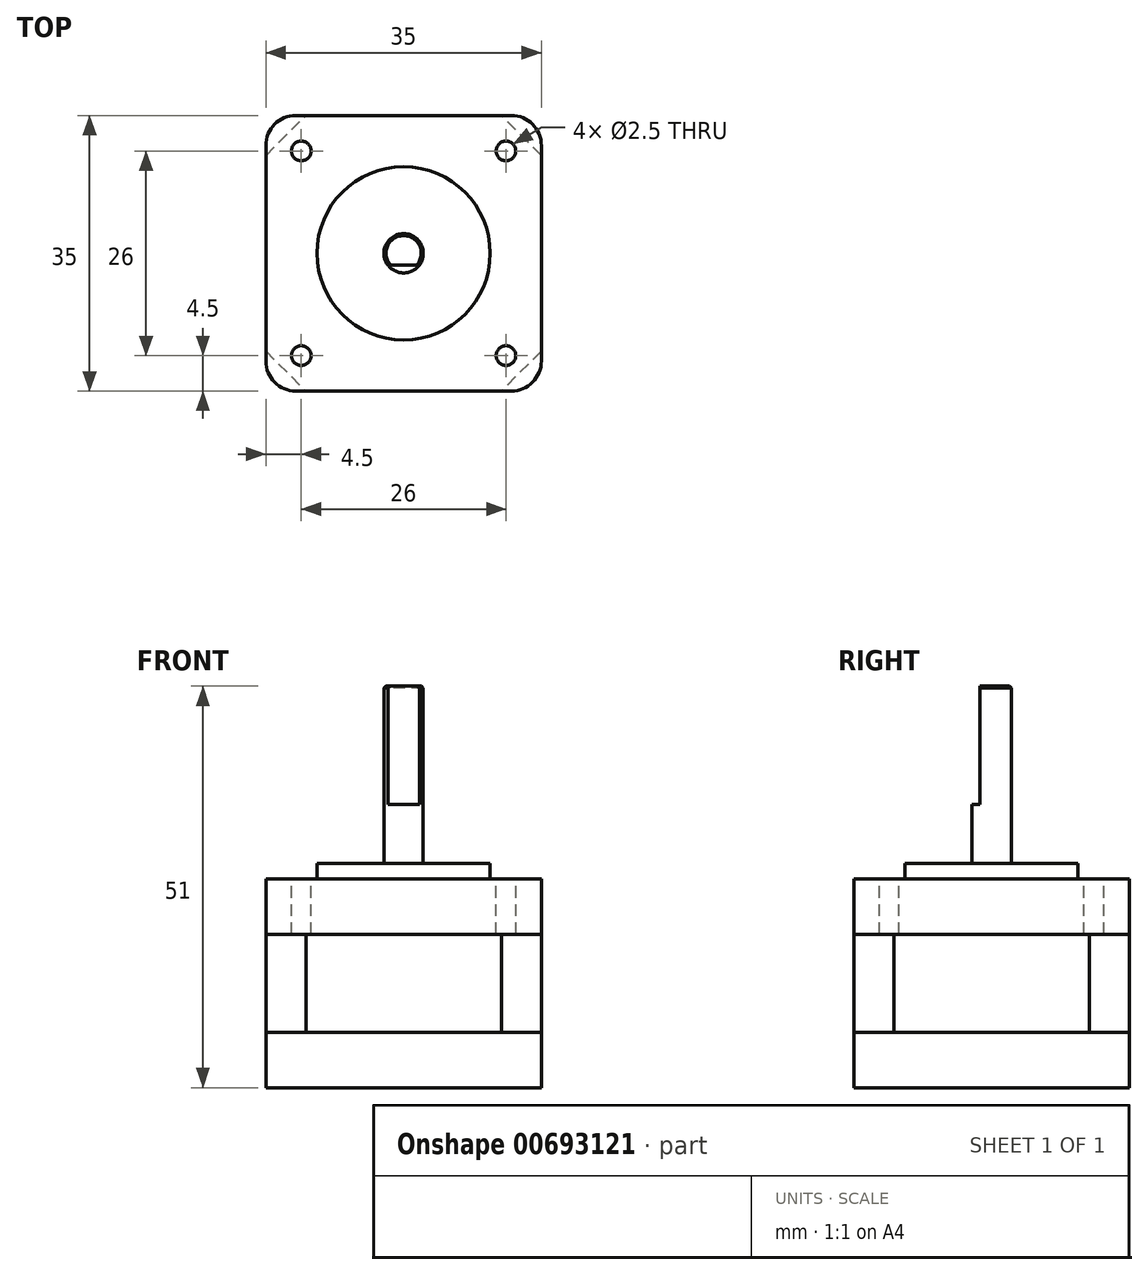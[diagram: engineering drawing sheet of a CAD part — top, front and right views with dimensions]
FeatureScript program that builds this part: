
annotation { "Feature Type Name" : "Feature", "Feature Type Description" : "" }
export const myFeature = defineFeature(function(context is Context, id is Id, definition is map)
    precondition{}
    {
        {
            var Q0;
            Q0=qCreatedBy(makeId("Top.planeOp"),FACE);
            var sketch = newSketch(context, id + "F0", { "sketchPlane" : qUnion([Q0])});
            skLineSegment(sketch, "E0.bottom", {"start": v(17.5, -17.5) * mm, "end": v(-17.5, -17.5) * mm});
            skLineSegment(sketch, "E0.top", {"start": v(17.5, 17.5) * mm, "end": v(-17.5, 17.5) * mm});
            skLineSegment(sketch, "E0.left", {"start": v(17.5, -17.5) * mm, "end": v(17.5, 17.5) * mm});
            skLineSegment(sketch, "E0.right", {"start": v(-17.5, -17.5) * mm, "end": v(-17.5, 17.5) * mm});
            skPoint(sketch, "E0.middle", {"position": v(0, 0) * mm});
            skPoint(sketch, "E1", {"position": v(-13, 13) * mm});
            skPoint(sketch, "E2.MirrorP", {"position": v(13, 13) * mm});
            skPoint(sketch, "E3.MirrorP", {"position": v(-13, -13) * mm});
            skPoint(sketch, "E4.MirrorP", {"position": v(13, -13) * mm});
            skCircle(sketch, "E5", {"center": v(0, 0) * mm, "radius": 11 * mm});
            skSolve(sketch);
        }
        {
            var Q0;
            Q0=makeQuery(id+"F0.imprint","IMPRINT",FACE,{"disambiguationData":[TD([[makeQuery(id+"F0.imprint","IMPRINT",EDGE,{"derivedFrom":sQuery(id+"F0.wireOp",EDGE,"E5")}),1.0]])]});
            extrude(context, id + "F1", {"entities" : qUnion([Q0]), "depth" : 2 * mm, "offsetDistance" : 25.4 * mm});
        }
        {
            var Q0;
            Q0=makeQuery(id+"F0.imprint","IMPRINT",FACE,{"disambiguationData":[TD([[makeQuery(id+"F0.imprint","IMPRINT",EDGE,{"derivedFrom":sQuery(id+"F0.wireOp",EDGE,"E5")}),1.0]])]});
            var Q1;
            Q1=makeQuery(id+"F0.imprint","IMPRINT",FACE,{"disambiguationData":[TD([[makeQuery(id+"F0.imprint","IMPRINT",EDGE,{"derivedFrom":sQuery(id+"F0.wireOp",EDGE,"E0.bottom")}),-1.0]])]});
            extrude(context, id + "F2", {"entities" : qUnion([Q0, Q1]), "operationType" : NewBodyOperationType.ADD, "oppositeDirection" : true, "depth" : 7 * mm, "offsetDistance" : 25.4 * mm});
        }
        {
            var Q0;
            Q0=makeQuery(id+"F2.opExtrude","CAP_FACE",FACE,{"disambiguationData":[OSD([sQuery(id+"F0.wireOp",EDGE,"E0.bottom"),sQuery(id+"F0.wireOp",EDGE,"E0.top"),sQuery(id+"F0.wireOp",EDGE,"E0.left"),sQuery(id+"F0.wireOp",EDGE,"E0.right")])],"isStart":false});
            extrude(context, id + "F3", {"entities" : qUnion([Q0]), "depth" : 12.5 * mm, "offsetDistance" : 25.4 * mm});
        }
        {
            var Q0;
            Q0=makeQuery(id+"F3.opExtrude","CAP_FACE",FACE,{"disambiguationData":[OSD([sQuery(id+"F0.wireOp",EDGE,"E0.bottom"),sQuery(id+"F0.wireOp",EDGE,"E0.top"),sQuery(id+"F0.wireOp",EDGE,"E0.left"),sQuery(id+"F0.wireOp",EDGE,"E0.right")])],"isStart":false});
            extrude(context, id + "F4", {"entities" : qUnion([Q0]), "depth" : 7 * mm, "offsetDistance" : 25.4 * mm});
        }
        {
            var Q0;
            Q0=makeQuery(id+"F3.opExtrude","SWEPT_EDGE",EDGE,{"disambiguationData":[OSD([sQuery(id+"F0.wireOp",EDGE,"E0.bottom"),sQuery(id+"F0.wireOp",EDGE,"E0.right")])]});
            var Q1;
            Q1=makeQuery(id+"F3.opExtrude","SWEPT_EDGE",EDGE,{"disambiguationData":[OSD([sQuery(id+"F0.wireOp",EDGE,"E0.bottom"),sQuery(id+"F0.wireOp",EDGE,"E0.left")])]});
            var Q2;
            Q2=makeQuery(id+"F3.opExtrude","SWEPT_EDGE",EDGE,{"disambiguationData":[OSD([sQuery(id+"F0.wireOp",EDGE,"E0.top"),sQuery(id+"F0.wireOp",EDGE,"E0.right")])]});
            var Q3;
            Q3=makeQuery(id+"F3.opExtrude","SWEPT_EDGE",EDGE,{"disambiguationData":[OSD([sQuery(id+"F0.wireOp",EDGE,"E0.top"),sQuery(id+"F0.wireOp",EDGE,"E0.left")])]});
            chamfer(context, id + "F5", {"entities" : qUnion([Q0, Q1, Q2, Q3]), "width" : 5.08 * mm, "tangentPropagation" : true});
        }
        {
            var Q0;
            Q0=makeQuery(id+"F2.opExtrude","SWEPT_EDGE",EDGE,{"disambiguationData":[OSD([sQuery(id+"F0.wireOp",EDGE,"E0.top"),sQuery(id+"F0.wireOp",EDGE,"E0.left")])]});
            var Q1;
            Q1=makeQuery(id+"F4.opExtrude","SWEPT_EDGE",EDGE,{"disambiguationData":[OSD([sQuery(id+"F0.wireOp",EDGE,"E0.top"),sQuery(id+"F0.wireOp",EDGE,"E0.left")])]});
            var Q2;
            Q2=makeQuery(id+"F2.opExtrude","SWEPT_EDGE",EDGE,{"disambiguationData":[OSD([sQuery(id+"F0.wireOp",EDGE,"E0.bottom"),sQuery(id+"F0.wireOp",EDGE,"E0.left")])]});
            var Q3;
            Q3=makeQuery(id+"F2.opExtrude","SWEPT_EDGE",EDGE,{"disambiguationData":[OSD([sQuery(id+"F0.wireOp",EDGE,"E0.bottom"),sQuery(id+"F0.wireOp",EDGE,"E0.right")])]});
            var Q4;
            Q4=makeQuery(id+"F4.opExtrude","SWEPT_EDGE",EDGE,{"disambiguationData":[OSD([sQuery(id+"F0.wireOp",EDGE,"E0.bottom"),sQuery(id+"F0.wireOp",EDGE,"E0.left")])]});
            var Q5;
            Q5=makeQuery(id+"F4.opExtrude","SWEPT_EDGE",EDGE,{"disambiguationData":[OSD([sQuery(id+"F0.wireOp",EDGE,"E0.bottom"),sQuery(id+"F0.wireOp",EDGE,"E0.right")])]});
            var Q6;
            Q6=makeQuery(id+"F4.opExtrude","SWEPT_EDGE",EDGE,{"disambiguationData":[OSD([sQuery(id+"F0.wireOp",EDGE,"E0.top"),sQuery(id+"F0.wireOp",EDGE,"E0.right")])]});
            var Q7;
            Q7=makeQuery(id+"F2.opExtrude","SWEPT_EDGE",EDGE,{"disambiguationData":[OSD([sQuery(id+"F0.wireOp",EDGE,"E0.top"),sQuery(id+"F0.wireOp",EDGE,"E0.right")])]});
            fillet(context, id + "F6", {"entities" : qUnion([Q0, Q1, Q2, Q3, Q4, Q5, Q6, Q7]), "radius" : 3.8 * mm, "tangentPropagation" : true, "allowEdgeOverflow" : false});
        }
        {
            var Q0;
            Q0=sQuery(id+"F0.wireOp",VERTEX,"E1");
            var Q1;
            Q1=sQuery(id+"F0.wireOp",VERTEX,"E2.MirrorP");
            var Q2;
            Q2=sQuery(id+"F0.wireOp",VERTEX,"E4.MirrorP");
            var Q3;
            Q3=sQuery(id+"F0.wireOp",VERTEX,"E3.MirrorP");
            var Q4;
            Q4=makeQuery(id+"F1.opExtrude","SWEPT_BODY",BODY,{"disambiguationData":[OSD([sQuery(id+"F0.wireOp",EDGE,"E5")])]});
            hole(context, id + "F7", {"style" : HoleStyle.SIMPLE, "endStyle" : HoleEndStyle.BLIND, "standardTappedOrClearance" : lookupTablePath({ "standard" : "ISO", "engagement" : "75%", "pitch" : "0.5 mm", "size" : "M3", "type" : "Tapped" }), "standardBlindInLast" : lookupTablePath({ "standard" : "ISO", "engagement" : "75%", "pitch" : "0.5 mm", "size" : "M3", "type" : "Tapped" }), "holeDiameter" : 2.5 * mm, "majorDiameter" : 3 * mm, "showTappedDepth" : true, "holeDepth" : 14.2 * mm, "isTappedThrough" : true, "tappedDepth" : 12.7 * mm, "tapClearance" : 3, "locations" : qUnion([Q0, Q1, Q2, Q3]), "scope" : qUnion([Q4])});
        }
        {
            var Q0;
            Q0=makeQuery(id+"F1.opExtrude","CAP_FACE",FACE,{"disambiguationData":[OSD([sQuery(id+"F0.wireOp",EDGE,"E5")])],"isStart":false});
            var sketch = newSketch(context, id + "F8", { "sketchPlane" : qUnion([Q0])});
            skCircle(sketch, "E6", {"center": v(0, 0) * mm, "radius": 2.5 * mm});
            skSolve(sketch);
        }
        {
            var Q0;
            Q0=makeQuery(id+"F8.imprint","IMPRINT",FACE,{"disambiguationData":[TD([[makeQuery(id+"F8.imprint","IMPRINT",EDGE,{"derivedFrom":sQuery(id+"F8.wireOp",EDGE,"E6")}),1.0]])]});
            extrude(context, id + "F9", {"entities" : qUnion([Q0]), "operationType" : NewBodyOperationType.ADD, "depth" : 7.5 * mm, "offsetDistance" : 25.4 * mm});
        }
        {
            var Q0;
            Q0=makeQuery(id+"F9.opExtrude","CAP_FACE",FACE,{"disambiguationData":[OSD([sQuery(id+"F8.wireOp",EDGE,"E6")])],"isStart":false});
            var sketch = newSketch(context, id + "F10", { "sketchPlane" : qUnion([Q0])});
            skArc(sketch, "E7", {"start": v(2, -1.5) * mm, "mid": v(0, 2.5) * mm, "end": v(-2, -1.5) * mm});
            skLineSegment(sketch, "E8", {"start": v(-2, -1.5) * mm, "end": v(2, -1.5) * mm});
            skSolve(sketch);
        }
        {
            var Q0;
            Q0=makeQuery(id+"F10.imprint","IMPRINT",FACE,{"disambiguationData":[TD([[makeQuery(id+"F10.imprint","IMPRINT",EDGE,{"derivedFrom":sQuery(id+"F10.wireOp",EDGE,"E7")}),1.0]])]});
            extrude(context, id + "F11", {"entities" : qUnion([Q0]), "operationType" : NewBodyOperationType.ADD, "depth" : 15 * mm, "offsetDistance" : 25.4 * mm});
        }
        {
            var Q0;
            Q0=makeQuery(id+"F11.opExtrude","CAP_EDGE",EDGE,{"disambiguationData":[OSD([sQuery(id+"F10.wireOp",EDGE,"E7")])],"isStart":false});
            chamfer(context, id + "F12", {"entities" : qUnion([Q0]), "width" : 0.25 * mm, "tangentPropagation" : true});
        }
    });
